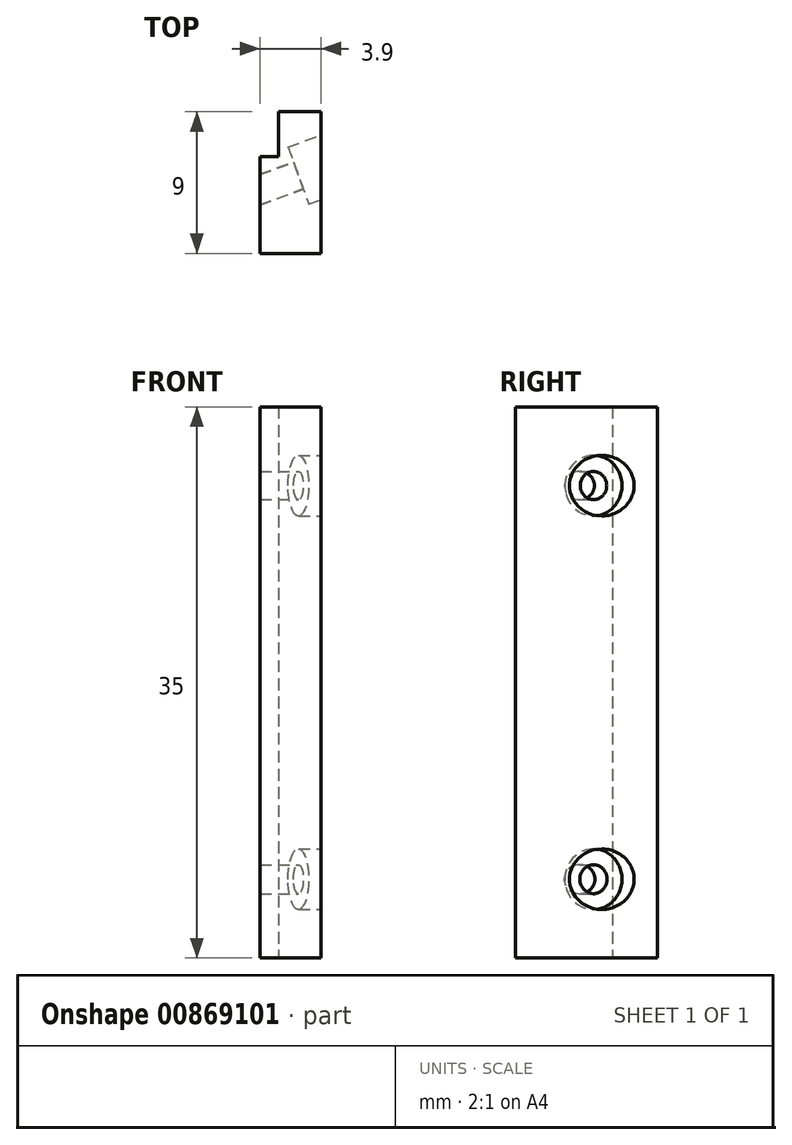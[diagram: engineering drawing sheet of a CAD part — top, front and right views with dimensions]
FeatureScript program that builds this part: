
annotation { "Feature Type Name" : "Feature", "Feature Type Description" : "" }
export const myFeature = defineFeature(function(context is Context, id is Id, definition is map)
    precondition{}
    {
        {
            var Q0;
            Q0=qCreatedBy(makeId("Top.planeOp"),FACE);
            var sketch = newSketch(context, id + "F0", { "sketchPlane" : qUnion([Q0])});
            skLineSegment(sketch, "E0", {"start": v(0, 0) * mm, "end": v(0, 2.85) * mm});
            skLineSegment(sketch, "E1", {"start": v(0, 2.85) * mm, "end": v(2.7, 2.85) * mm});
            skLineSegment(sketch, "E2", {"start": v(2.7, 2.85) * mm, "end": v(2.7, -6.15) * mm});
            skLineSegment(sketch, "E3", {"start": v(2.7, -6.15) * mm, "end": v(-1.2, -6.15) * mm});
            skLineSegment(sketch, "E4", {"start": v(-1.2, 0) * mm, "end": v(0, 0) * mm});
            skPoint(sketch, "E5.end.orphan", {"position": v(-1.2, 0) * mm});
            skLineSegment(sketch, "E6", {"start": v(-1.2, 0) * mm, "end": v(-1.2, -6.15) * mm});
            skSolve(sketch);
        }
        {
            var Q0;
            Q0 = qSketchRegion(id + "F0", true);
            extrude(context, id + "F1", {"entities" : qUnion([Q0]), "depth" : 35 * mm, "offsetDistance" : 25 * mm});
        }
        {
            var Q0;
            Q0=makeQuery(id+"F1.opExtrude","SWEPT_EDGE",EDGE,{"disambiguationData":[OSD([sQuery(id+"F0.wireOp",EDGE,"E1"),sQuery(id+"F0.wireOp",EDGE,"E2")])]});
            cPlane(context, id + "F2", {"entities" : qUnion([Q0]), "cplaneType" : CPlaneType.LINE_ANGLE, "offset" : 0 * mm, "angle" : 160 * degree, "width" : 150 * mm, "height" : 150 * mm});
        }
        {
            var Q0;
            Q0=qCreatedBy(id+"F2.planeOp",FACE);
            var sketch = newSketch(context, id + "F3", { "sketchPlane" : qUnion([Q0])});
            skLineSegment(sketch, "E7.0", {"start": v(1.75, 35) * mm, "end": v(1.75, 0) * mm});
            skPoint(sketch, "E8", {"position": v(1.75, 17.5) * mm});
            skLineSegment(sketch, "E9", {"start": v(1.75, 17.5) * mm, "end": v(-1.56, 17.5) * mm, "construction": true});
            skCircle(sketch, "E10", {"center": v(-1.56, 30) * mm, "radius": 0.9 * mm});
            skCircle(sketch, "E11", {"center": v(-1.56, 5) * mm, "radius": 0.92 * mm});
            skLineSegment(sketch, "E12", {"start": v(-1.56, 30) * mm, "end": v(-1.56, 5) * mm, "construction": true});
            skPoint(sketch, "E13", {"position": v(-1.56, 17.5) * mm});
            skSolve(sketch);
        }
        {
            var Q0;
            Q0 = qSketchRegion(id + "F3", true);
            extrude(context, id + "F4", {"entities" : qUnion([Q0]), "operationType" : NewBodyOperationType.REMOVE, "endBound" : BoundingType.THROUGH_ALL, "oppositeDirection" : true, "depth" : 25 * mm, "offsetDistance" : 25 * mm});
        }
        {
            var Q0;
            Q0=qCreatedBy(id+"F2.planeOp",FACE);
            var sketch = newSketch(context, id + "F5", { "sketchPlane" : qUnion([Q0])});
            skPoint(sketch, "E14.0", {"position": v(-1.56, 17.5) * mm});
            skCircle(sketch, "E15", {"center": v(-1.56, 30) * mm, "radius": 1.93 * mm});
            skPoint(sketch, "E16.0", {"position": v(-1.56, 5) * mm});
            skCircle(sketch, "E17", {"center": v(-1.56, 5) * mm, "radius": 1.93 * mm});
            skSolve(sketch);
        }
        {
            var Q0;
            Q0 = qSketchRegion(id + "F5", true);
            extrude(context, id + "F6", {"entities" : qUnion([Q0]), "operationType" : NewBodyOperationType.REMOVE, "oppositeDirection" : true, "depth" : 2.75 * mm, "offsetDistance" : 25 * mm});
        }
    });
